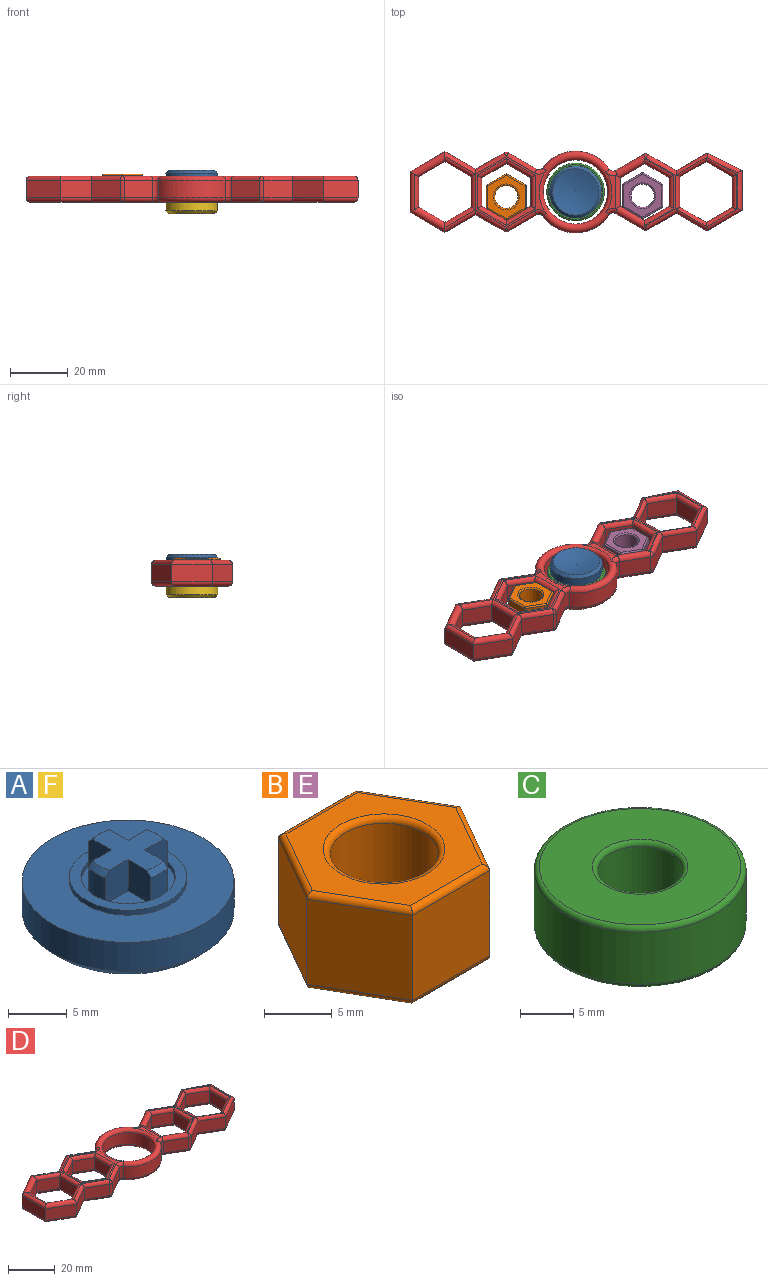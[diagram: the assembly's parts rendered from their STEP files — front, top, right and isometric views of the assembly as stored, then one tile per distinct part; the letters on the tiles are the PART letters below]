
ASSEMBLY  parts=6 mates=5
PART A: 25 faces, bbox 18x18x7.2 mm
  f0: cone r=9mm half-angle=45deg, axis (0,0,1), area 72.9mm2, adj f1,f3
  f1: cylinder r=9mm len=18mm, axis (0,0,-1), area 169.6mm2, adj f0,f2
  f2: plane 18x18mm, normal (0,0,1), area 176.5mm2, adj f1,f5
  f3: revolved ~0x0mm, area 0mm2, adj f0
  f4: cylinder r=4mm len=8mm, axis (0,0,-1), area 12.6mm2, adj f6,f24
  f5: cylinder r=4.98mm len=9.96mm, axis (0,0,-1), area 15.7mm2, adj f2,f6
  f6: plane 9.96x9.96mm, normal (0,0,1), area 27.7mm2, adj f4,f5
  f7: cone r=3.38mm half-angle=45deg, axis (0,0,-1), area 1.4mm2, adj f10,f13,f14,f15
  f8: cone r=3.38mm half-angle=45deg, axis (0,0,-1), area 1.4mm2, adj f10,f16,f17,f18
  f9: cone r=3.38mm half-angle=45deg, axis (0,0,-1), area 1.4mm2, adj f10,f19,f20,f21
  f10: plane 6.75x6.75mm, normal (0,0,1), area 22.6mm2, adj f7,f8,f9,f11,f12,f13,f15,f16
  f11: cone r=3.38mm half-angle=45deg, axis (0,0,-1), area 1.4mm2, adj f10,f12,f22,f23
  f12: plane 3.26x2.75mm, normal (-1,0,0), area 8.8mm2, adj f10,f11,f13,f23,f24
  f13: plane 3.26x2.75mm, normal (0,1,0), area 8.8mm2, adj f7,f10,f12,f14,f24
  f14: cylinder r=3.88mm len=2.75mm, axis (0,0,-1), area 5.6mm2, adj f7,f13,f15,f24
  f15: plane 3.26x2.75mm, normal (0,-1,0), area 8.8mm2, adj f7,f10,f14,f16,f24
  f16: plane 3.26x2.75mm, normal (-1,0,0), area 8.8mm2, adj f8,f10,f15,f17,f24
  f17: cylinder r=3.88mm len=2.75mm, axis (0,0,-1), area 5.6mm2, adj f8,f16,f18,f24
  f18: plane 3.26x2.75mm, normal (1,0,0), area 8.8mm2, adj f8,f10,f17,f19,f24
  f19: plane 3.26x2.75mm, normal (0,-1,0), area 8.8mm2, adj f9,f10,f18,f20,f24
  f20: cylinder r=3.88mm len=2.75mm, axis (0,0,-1), area 5.6mm2, adj f9,f19,f21,f24
  f21: plane 3.26x2.75mm, normal (0,1,0), area 8.8mm2, adj f9,f10,f20,f22,f24
  f22: plane 3.26x2.75mm, normal (1,0,0), area 8.8mm2, adj f10,f11,f21,f23,f24
  f23: cylinder r=3.88mm len=2.75mm, axis (0,0,-1), area 5.6mm2, adj f11,f12,f22,f24
  f24: plane 8x8mm, normal (0,0,1), area 23.6mm2, adj f4,f12,f13,f14,f15,f16,f17,f18
PART B: 23 faces, bbox 16.2x14x8.7 mm
  f0: plane 7.7x6.99mm, normal (0.86,0.5,0), area 62.2mm2, adj f1,f6,f11,f18
  f1: plane 8.08x7.7mm, normal (0,1,0), area 62.2mm2, adj f0,f2,f10,f17
  f2: plane 7.7x7.01mm, normal (-0.87,0.5,0), area 62.2mm2, adj f1,f3,f12,f19
  f3: plane 7.7x6.99mm, normal (-0.86,-0.5,0), area 62.2mm2, adj f2,f4,f14,f21
  f4: plane 8.08x7.7mm, normal (0,-1,0), area 62.2mm2, adj f3,f6,f15,f22
  f5: cylinder r=4mm len=8mm, axis (0,0,-1), area 193.5mm2, adj f9,f16
  f6: plane 7.7x7.01mm, normal (0.87,-0.5,0), area 62.2mm2, adj f0,f4,f13,f20
  f7: plane 15.01x13.02mm, normal (0,0,1), area 82.7mm2, adj f16,f17,f18,f19,f20,f21,f22
  f8: plane 15.01x13.02mm, normal (0,0,-1), area 82.7mm2, adj f9,f10,f11,f12,f13,f14,f15
  f9: torus R=4.5mm, axis (0,0,1), area 20.6mm2, adj f5,f8
  f10: cylinder r=0.5mm len=8.08mm, axis (-1,0,0), area 6.2mm2, adj f1,f8,f11,f12
  f11: cylinder r=0.5mm len=7.24mm, axis (-0.5,0.86,0), area 6.2mm2, adj f0,f8,f10,f13
  f12: cylinder r=0.5mm len=7.26mm, axis (-0.5,-0.87,0), area 6.2mm2, adj f2,f8,f10,f14
  f13: cylinder r=0.5mm len=7.26mm, axis (0.5,0.87,0), area 6.2mm2, adj f6,f8,f11,f15
  f14: cylinder r=0.5mm len=7.24mm, axis (0.5,-0.86,0), area 6.2mm2, adj f3,f8,f12,f15
  f15: cylinder r=0.5mm len=8.08mm, axis (1,0,0), area 6.2mm2, adj f4,f8,f13,f14
  f16: torus R=4.5mm, axis (0,0,1), area 20.6mm2, adj f5,f7
  f17: cylinder r=0.5mm len=8.08mm, axis (1,0,0), area 6.2mm2, adj f1,f7,f18,f19
  f18: cylinder r=0.5mm len=7.24mm, axis (0.5,-0.86,0), area 6.2mm2, adj f0,f7,f17,f20
  f19: cylinder r=0.5mm len=7.26mm, axis (0.5,0.87,0), area 6.2mm2, adj f2,f7,f17,f21
  f20: cylinder r=0.5mm len=7.26mm, axis (-0.5,-0.87,0), area 6.2mm2, adj f6,f7,f18,f22
  f21: cylinder r=0.5mm len=7.24mm, axis (-0.5,0.86,0), area 6.2mm2, adj f3,f7,f19,f22
  f22: cylinder r=0.5mm len=8.08mm, axis (-1,0,0), area 6.2mm2, adj f4,f7,f20,f21
PART C: 8 faces, bbox 21.6x21.6x7 mm
  f0: cylinder r=4mm len=8mm, axis (0,0,-1), area 150.8mm2, adj f4,f6
  f1: cylinder r=10mm len=20mm, axis (0,0,-1), area 377mm2, adj f5,f7
  f2: plane 19x19mm, normal (0,0,1), area 219.9mm2, adj f6,f7
  f3: plane 19x19mm, normal (0,0,-1), area 219.9mm2, adj f4,f5
  f4: torus R=4.5mm, axis (0,0,1), area 20.6mm2, adj f0,f3
  f5: torus R=9.5mm, axis (0,0,1), area 48.5mm2, adj f1,f3
  f6: torus R=4.5mm, axis (0,0,1), area 20.6mm2, adj f0,f2
  f7: torus R=9.5mm, axis (0,0,1), area 48.5mm2, adj f1,f2
PART D: 155 faces, bbox 115.1x30.6x9 mm
  f0: plane 24.54x24.41mm, normal (0,0,1), area 61.3mm2, adj f61,f68,f76,f78,f84,f89,f91,f101
  f1: plane 14x4mm, normal (0,0,1), area 21.5mm2, adj f85,f91,f94,f115,f130,f131
  f2: plane 15.94x7.29mm, normal (0,0,1), area 6mm2, adj f92,f105,f106,f107,f121
  f3: plane 24.54x24.41mm, normal (0,0,-1), area 61.3mm2, adj f64,f70,f80,f81,f87,f98,f99,f114
  f4: plane 15.94x7.29mm, normal (0,0,-1), area 6mm2, adj f93,f108,f109,f110,f122
  f5: plane 14x4mm, normal (0,0,-1), area 21.5mm2, adj f86,f97,f98,f128,f136,f137
  f6: plane 9.13x6mm, normal (0.5,-0.87,0), area 63.2mm2, adj f7,f50,f53,f56
  f7: plane 9.13x6mm, normal (-0.5,-0.87,0), area 63.2mm2, adj f6,f8,f55,f57
  f8: plane 10.54x6mm, normal (-1,0,0), area 63.2mm2, adj f7,f9,f61,f64
  f9: plane 9.13x6mm, normal (-0.5,0.87,0), area 63.2mm2, adj f8,f10,f67,f71
  f10: plane 9.13x6mm, normal (0.5,0.87,0), area 63.2mm2, adj f9,f50,f60,f65
  f11: plane 9.13x6mm, normal (0.5,-0.87,0), area 63.2mm2, adj f12,f45,f118,f125
  f12: plane 9.13x6mm, normal (-0.5,-0.87,0), area 63.2mm2, adj f11,f13,f105,f110
  f13: plane 10.54x6mm, normal (-1,0,0), area 63.2mm2, adj f12,f14,f106,f109
  f14: plane 9.13x6mm, normal (-0.5,0.87,0), area 63.2mm2, adj f13,f15,f120,f123
  f15: plane 9.13x6mm, normal (0.5,0.87,0), area 63.2mm2, adj f14,f45,f119,f124
  f16: plane 8.5x6mm, normal (-0.5,0.87,0), area 58.9mm2, adj f17,f46,f116,f127
  f17: plane 8.5x6mm, normal (0.5,0.87,0), area 58.9mm2, adj f16,f18,f131,f136
  f18: plane 9.82x6mm, normal (1,0,0), area 58.9mm2, adj f17,f19,f115,f128
  f19: plane 8.5x6mm, normal (0.5,-0.87,0), area 58.9mm2, adj f18,f20,f94,f97
  f20: plane 8.5x6mm, normal (-0.5,-0.87,0), area 58.9mm2, adj f19,f46,f90,f95
  f21: plane 9.82x6mm, normal (1,0,0), area 58.9mm2, adj f22,f47,f146,f152
  f22: plane 8.5x6mm, normal (0.5,-0.87,0), area 58.9mm2, adj f21,f23,f144,f150
  f23: plane 8.5x6mm, normal (-0.5,-0.87,0), area 58.9mm2, adj f22,f24,f143,f149
  f24: plane 9.82x6mm, normal (-1,0,0), area 58.9mm2, adj f23,f25,f145,f151
  f25: plane 8.5x6mm, normal (-0.5,0.87,0), area 58.9mm2, adj f24,f47,f147,f153
  f26: plane 9.81x6mm, normal (-0.5,-0.87,0), area 68mm2, adj f129,f131,f136,f142
  f27: plane 9.88x6mm, normal (0.5,-0.87,0), area 68.4mm2, adj f28,f138,f139,f142
  f28: plane 10.63x6.13mm, normal (-0.5,-0.87,0), area 73.6mm2, adj f27,f29,f133,f134
  f29: plane 12.13x7mm, normal (0.5,-0.87,0), area 84mm2, adj f28,f30,f121,f122
  f30: plane 14x6mm, normal (1,0,0), area 84mm2, adj f29,f31,f107,f108
  f31: plane 12.13x6mm, normal (0.44,0.9,0), area 81mm2, adj f30,f32,f92,f93
  f32: plane 10.63x6.13mm, normal (-0.5,0.87,0), area 73.6mm2, adj f31,f33,f104,f111
  f33: plane 9.88x6mm, normal (0.5,0.87,0), area 68.4mm2, adj f32,f96,f117,f126
  f34: plane 9.81x6mm, normal (-0.5,0.87,0), area 68mm2, adj f77,f94,f96,f97
  f35: cylinder r=14.12mm len=23.19mm, axis (0,0,-1), area 163.2mm2, adj f77,f79,f91,f98
  f36: plane 9.85x6mm, normal (0.5,0.87,0), area 68.3mm2, adj f69,f78,f79,f80
  f37: plane 9.88x6mm, normal (-0.5,0.87,0), area 68.4mm2, adj f38,f68,f69,f70
  f38: plane 10.63x6.13mm, normal (0.5,0.87,0), area 73.6mm2, adj f37,f39,f62,f63
  f39: plane 12.13x7mm, normal (-0.5,0.87,0), area 84mm2, adj f38,f40,f53,f56
  f40: plane 14x6mm, normal (-1,0,0), area 84mm2, adj f39,f41,f59,f66
  f41: plane 12.13x7mm, normal (-0.5,-0.87,0), area 84mm2, adj f40,f42,f60,f65
  f42: plane 10.63x6.13mm, normal (0.5,-0.87,0), area 73.6mm2, adj f41,f43,f72,f75
  f43: plane 9.88x6mm, normal (-0.5,-0.87,0), area 68.4mm2, adj f42,f76,f81,f82
  f44: plane 9.85x6mm, normal (0.5,-0.87,0), area 68.3mm2, adj f82,f89,f99,f100
  f45: plane 10.54x6mm, normal (1,0,0), area 63.2mm2, adj f11,f15,f132,f135
  f46: plane 9.82x6mm, normal (-1,0,0), area 58.9mm2, adj f16,f20,f102,f113
  f47: plane 8.5x6mm, normal (0.5,0.87,0), area 58.9mm2, adj f21,f25,f148,f154
  f48: cylinder r=14.12mm len=23.19mm, axis (0,0,-1), area 163.2mm2, adj f91,f98,f100,f129
  f49: cylinder r=11.12mm len=22.25mm, axis (0,0,-1), area 419.4mm2, adj f91,f98
  f50: plane 10.54x6mm, normal (1,0,0), area 63.2mm2, adj f6,f10,f54,f58
  f51: plane 23.46x10.63mm, normal (0,0,1), area 14.5mm2, adj f90,f94,f102,f116,f117,f131,f132,f138
  f52: plane 23.46x10.63mm, normal (0,0,-1), area 14.5mm2, adj f95,f97,f113,f126,f127,f135,f136,f139
  f53: cylinder r=1.5mm len=13.63mm, axis (-0.87,-0.5,0), area 57.8mm2, adj f6,f39,f54,f55,f59,f62
  f54: cylinder r=1.5mm len=12.27mm, axis (0,-1,0), area 26.3mm2, adj f50,f53,f59,f60
  f55: cylinder r=1.5mm len=11.38mm, axis (-0.87,0.5,0), area 26.3mm2, adj f7,f53,f61,f62
  f56: cylinder r=1.5mm len=13.63mm, axis (0.87,0.5,0), area 57.8mm2, adj f6,f39,f57,f58,f63,f66
  f57: cylinder r=1.5mm len=11.38mm, axis (0.87,-0.5,0), area 26.3mm2, adj f7,f56,f63,f64
  f58: cylinder r=1.5mm len=12.27mm, axis (0,1,0), area 26.3mm2, adj f50,f56,f65,f66
  f59: cylinder r=1.5mm len=14mm, axis (0,1,0), area 31.5mm2, adj f40,f53,f54,f60
  f60: cylinder r=1.5mm len=13.63mm, axis (0.87,-0.5,0), area 57.8mm2, adj f10,f41,f54,f59,f67,f72
  f61: cylinder r=1.5mm len=12.27mm, axis (0,1,0), area 26.3mm2, adj f0,f8,f55,f67
  f62: cylinder r=1.5mm len=12.13mm, axis (0.87,-0.5,0), area 28.9mm2, adj f38,f53,f55,f68
  f63: cylinder r=1.5mm len=12.13mm, axis (-0.87,0.5,0), area 28.9mm2, adj f38,f56,f57,f70
  f64: cylinder r=1.5mm len=12.27mm, axis (0,-1,0), area 26.3mm2, adj f3,f8,f57,f71
  f65: cylinder r=1.5mm len=13.63mm, axis (-0.87,0.5,0), area 57.8mm2, adj f10,f41,f58,f66,f71,f75
  f66: cylinder r=1.5mm len=14mm, axis (0,-1,0), area 31.5mm2, adj f40,f56,f58,f65
  f67: cylinder r=1.5mm len=11.38mm, axis (0.87,0.5,0), area 26.3mm2, adj f9,f60,f61,f72
  f68: cylinder r=1.5mm len=11.38mm, axis (0.87,0.5,0), area 27.6mm2, adj f0,f37,f62,f73
  f69: cylinder r=1.5mm len=6mm, axis (0,0,-1), area 9.4mm2, adj f36,f37,f73,f74
  f70: cylinder r=1.5mm len=11.38mm, axis (-0.87,-0.5,0), area 27.6mm2, adj f3,f37,f63,f74
  f71: cylinder r=1.5mm len=11.38mm, axis (-0.87,-0.5,0), area 26.3mm2, adj f9,f64,f65,f75
  f72: cylinder r=1.5mm len=12.13mm, axis (-0.87,-0.5,0), area 28.9mm2, adj f42,f60,f67,f76
  f73: sphere r=1.5mm, area 2.4mm2, adj f68,f69,f78
  f74: sphere r=1.5mm, area 2.4mm2, adj f69,f70,f80
  f75: cylinder r=1.5mm len=12.13mm, axis (0.87,0.5,0), area 28.9mm2, adj f42,f65,f71,f81
  f76: cylinder r=1.5mm len=11.38mm, axis (-0.87,0.5,0), area 27.6mm2, adj f0,f43,f72,f83
  f77: cylinder r=1.5mm len=6mm, axis (0,0,-1), area 13.6mm2, adj f34,f35,f85,f86
  f78: cylinder r=1.5mm len=10.6mm, axis (0.87,-0.5,0), area 26.8mm2, adj f0,f36,f73,f84
  f79: cylinder r=1.5mm len=6mm, axis (0,0,-1), area 13.2mm2, adj f35,f36,f84,f87
  f80: cylinder r=1.5mm len=10.6mm, axis (-0.87,0.5,0), area 26.8mm2, adj f3,f36,f74,f87
  f81: cylinder r=1.5mm len=11.38mm, axis (0.87,-0.5,0), area 27.6mm2, adj f3,f43,f75,f88
  f82: cylinder r=1.5mm len=6mm, axis (0,0,1), area 9.4mm2, adj f43,f44,f83,f88
  f83: sphere r=1.5mm, area 2.4mm2, adj f76,f82,f89
  f84: torus R=3mm, axis (0,0,1), area 7.1mm2, adj f0,f78,f79,f91
  f85: torus R=3mm, axis (0,0,1), area 7.3mm2, adj f1,f77,f91,f94
  f86: torus R=3mm, axis (0,0,1), area 7.3mm2, adj f5,f77,f97,f98
  f87: torus R=3mm, axis (0,0,1), area 7.1mm2, adj f3,f79,f80,f98
  f88: sphere r=1.5mm, area 2.4mm2, adj f81,f82,f99
  f89: cylinder r=1.5mm len=10.6mm, axis (-0.87,-0.5,0), area 26.8mm2, adj f0,f44,f83,f101
  f90: cylinder r=1.5mm len=10.75mm, axis (-0.87,0.5,0), area 24.6mm2, adj f20,f51,f94,f102
  f91: torus R=12.62mm, axis (0,0,1), area 296mm2, adj f0,f1,f35,f48,f49,f84,f85,f101
  f92: cylinder r=1.5mm len=12.78mm, axis (0.9,-0.44,0), area 30.1mm2, adj f2,f31,f104,f105,f107
  f93: cylinder r=1.5mm len=12.78mm, axis (-0.9,0.44,0), area 30.1mm2, adj f4,f31,f108,f110,f111
  f94: cylinder r=1.5mm len=11.81mm, axis (0.87,0.5,0), area 51.3mm2, adj f1,f19,f34,f51,f85,f90,f103,f115
  f95: cylinder r=1.5mm len=10.75mm, axis (0.87,-0.5,0), area 24.6mm2, adj f20,f52,f97,f113
  f96: cylinder r=1.5mm len=6mm, axis (0,0,1), area 9.4mm2, adj f33,f34,f103,f112
  f97: cylinder r=1.5mm len=11.81mm, axis (-0.87,-0.5,0), area 51.3mm2, adj f5,f19,f34,f52,f86,f95,f112,f128
  f98: torus R=12.62mm, axis (0,0,1), area 296mm2, adj f3,f5,f35,f48,f49,f86,f87,f114
  f99: cylinder r=1.5mm len=10.6mm, axis (0.87,0.5,0), area 26.8mm2, adj f3,f44,f88,f114
  f100: cylinder r=1.5mm len=6mm, axis (0,0,-1), area 13.2mm2, adj f44,f48,f101,f114
  f101: torus R=3mm, axis (0,0,1), area 7.1mm2, adj f0,f89,f91,f100
  f102: cylinder r=1.5mm len=11.55mm, axis (0,1,0), area 24.6mm2, adj f46,f51,f90,f116
  f103: sphere r=1.5mm, area 2.4mm2, adj f94,f96,f117
  f104: cylinder r=1.5mm len=11.9mm, axis (0.87,0.5,0), area 25.1mm2, adj f32,f92,f105,f117,f118
  f105: cylinder r=1.5mm len=11.22mm, axis (-0.87,0.5,0), area 26mm2, adj f2,f12,f92,f104,f106,f118
  f106: cylinder r=1.5mm len=12.18mm, axis (0,1,0), area 26.3mm2, adj f2,f13,f105,f120,f121
  f107: cylinder r=1.5mm len=14mm, axis (0,-1,0), area 31.4mm2, adj f2,f30,f92,f121
  f108: cylinder r=1.5mm len=14mm, axis (0,1,0), area 31.4mm2, adj f4,f30,f93,f122
  f109: cylinder r=1.5mm len=12.18mm, axis (0,-1,0), area 26.3mm2, adj f4,f13,f110,f122,f123
  f110: cylinder r=1.5mm len=11.22mm, axis (0.87,-0.5,0), area 26mm2, adj f4,f12,f93,f109,f111,f125
  f111: cylinder r=1.5mm len=11.9mm, axis (-0.87,-0.5,0), area 25.1mm2, adj f32,f93,f110,f125,f126
  f112: sphere r=1.5mm, area 2.4mm2, adj f96,f97,f126
  f113: cylinder r=1.5mm len=11.55mm, axis (0,-1,0), area 24.6mm2, adj f46,f52,f95,f127
  f114: torus R=3mm, axis (0,0,1), area 7.1mm2, adj f3,f98,f99,f100
  f115: cylinder r=1.5mm len=11.55mm, axis (0,-1,0), area 24.6mm2, adj f1,f18,f94,f131
  f116: cylinder r=1.5mm len=10.75mm, axis (0.87,0.5,0), area 24.6mm2, adj f16,f51,f102,f131
  f117: cylinder r=1.5mm len=11.22mm, axis (0.87,-0.5,0), area 27.6mm2, adj f33,f51,f103,f104,f132
  f118: cylinder r=1.5mm len=10.91mm, axis (-0.87,-0.5,0), area 22.5mm2, adj f11,f104,f105,f132
  f119: cylinder r=1.5mm len=10.91mm, axis (0.87,-0.5,0), area 22.5mm2, adj f15,f120,f132,f133
  f120: cylinder r=1.5mm len=11.06mm, axis (0.87,0.5,0), area 24.4mm2, adj f14,f106,f119,f121,f133
  f121: cylinder r=1.5mm len=12.88mm, axis (-0.87,-0.5,0), area 29.7mm2, adj f2,f29,f106,f107,f120,f133
  f122: cylinder r=1.5mm len=12.88mm, axis (0.87,0.5,0), area 29.7mm2, adj f4,f29,f108,f109,f123,f134
  f123: cylinder r=1.5mm len=11.06mm, axis (-0.87,-0.5,0), area 24.4mm2, adj f14,f109,f122,f124,f134
  f124: cylinder r=1.5mm len=10.91mm, axis (-0.87,0.5,0), area 22.5mm2, adj f15,f123,f134,f135
  f125: cylinder r=1.5mm len=10.91mm, axis (0.87,0.5,0), area 22.5mm2, adj f11,f110,f111,f135
  f126: cylinder r=1.5mm len=11.22mm, axis (-0.87,0.5,0), area 27.6mm2, adj f33,f52,f111,f112,f135
  f127: cylinder r=1.5mm len=10.75mm, axis (-0.87,-0.5,0), area 24.6mm2, adj f16,f52,f113,f136
  f128: cylinder r=1.5mm len=11.55mm, axis (0,1,0), area 24.6mm2, adj f5,f18,f97,f136
  f129: cylinder r=1.5mm len=6mm, axis (0,0,-1), area 13.6mm2, adj f26,f48,f130,f137
  f130: torus R=3mm, axis (0,0,1), area 7.3mm2, adj f1,f91,f129,f131
  f131: cylinder r=1.5mm len=11.81mm, axis (0.87,-0.5,0), area 51.3mm2, adj f1,f17,f26,f51,f115,f116,f130,f140
  f132: cylinder r=1.5mm len=11.91mm, axis (0,-1,0), area 26.2mm2, adj f45,f51,f117,f118,f119,f138
  f133: cylinder r=1.5mm len=11.89mm, axis (-0.87,0.5,0), area 25.1mm2, adj f28,f119,f120,f121,f138
  f134: cylinder r=1.5mm len=11.89mm, axis (0.87,-0.5,0), area 25.1mm2, adj f28,f122,f123,f124,f139
  f135: cylinder r=1.5mm len=11.91mm, axis (0,1,0), area 26.2mm2, adj f45,f52,f124,f125,f126,f139
  f136: cylinder r=1.5mm len=11.81mm, axis (-0.87,0.5,0), area 51.3mm2, adj f5,f17,f26,f52,f127,f128,f137,f141
  f137: torus R=3mm, axis (0,0,1), area 7.3mm2, adj f5,f98,f129,f136
  f138: cylinder r=1.5mm len=11.22mm, axis (-0.87,-0.5,0), area 27.6mm2, adj f27,f51,f132,f133,f140
  f139: cylinder r=1.5mm len=11.22mm, axis (0.87,0.5,0), area 27.6mm2, adj f27,f52,f134,f135,f141
  f140: sphere r=1.5mm, area 2.4mm2, adj f131,f138,f142
  f141: sphere r=1.5mm, area 2.4mm2, adj f136,f139,f142
  f142: cylinder r=1.5mm len=6mm, axis (0,0,-1), area 9.4mm2, adj f26,f27,f140,f141
  f143: cylinder r=1.5mm len=10.75mm, axis (0.87,-0.5,0), area 24.6mm2, adj f3,f23,f144,f145
  f144: cylinder r=1.5mm len=10.75mm, axis (0.87,0.5,0), area 24.6mm2, adj f3,f22,f143,f146
  f145: cylinder r=1.5mm len=11.55mm, axis (0,-1,0), area 24.6mm2, adj f3,f24,f143,f147
  f146: cylinder r=1.5mm len=11.55mm, axis (0,1,0), area 24.6mm2, adj f3,f21,f144,f148
  f147: cylinder r=1.5mm len=10.75mm, axis (-0.87,-0.5,0), area 24.6mm2, adj f3,f25,f145,f148
  f148: cylinder r=1.5mm len=10.75mm, axis (-0.87,0.5,0), area 24.6mm2, adj f3,f47,f146,f147
  f149: cylinder r=1.5mm len=10.75mm, axis (-0.87,0.5,0), area 24.6mm2, adj f0,f23,f150,f151
  f150: cylinder r=1.5mm len=10.75mm, axis (-0.87,-0.5,0), area 24.6mm2, adj f0,f22,f149,f152
  f151: cylinder r=1.5mm len=11.55mm, axis (0,1,0), area 24.6mm2, adj f0,f24,f149,f153
  f152: cylinder r=1.5mm len=11.55mm, axis (0,-1,0), area 24.6mm2, adj f0,f21,f150,f154
  f153: cylinder r=1.5mm len=10.75mm, axis (0.87,0.5,0), area 24.6mm2, adj f0,f25,f151,f154
  f154: cylinder r=1.5mm len=10.75mm, axis (0.87,-0.5,0), area 24.6mm2, adj f0,f47,f152,f153
PART E: same geometry as B
PART F: same geometry as A
PLACE A rot(axis=(1,0,0),180deg) t=(-33.06,11.01,-0.49)mm
PLACE B rot(axis=(0,0,-1),150.1deg) t=(-57.06,9.28,-10.49)mm
PLACE C t=(-33.06,11.01,-11.49)mm
PLACE D t=(-33.06,11.01,-11.49)mm
PLACE E rot(axis=(0,0,1),89.9deg) t=(-9.81,9.71,-11.34)mm
PLACE F t=(-33.06,11.01,-15.49)mm
MATE fastened E.f2 <-> D.f17  axis (-0.5,-0.87,0) through (-13.31,3.65,-6.99)mm
MATE fastened F.f0 <-> C.f0  axis (0,0,1) through (-33.06,11.01,-11.49)mm
MATE fastened B.f1 <-> D.f25  axis (0.5,-0.87,0) through (-57.06,1.2,-9.99)mm
MATE fastened C.f0 <-> D.f35  axis (0,0,1) through (-33.06,11.01,-4.49)mm
MATE fastened A.f0 <-> C.f0  axis (0,0,-1) through (-33.06,11.01,-4.49)mm
